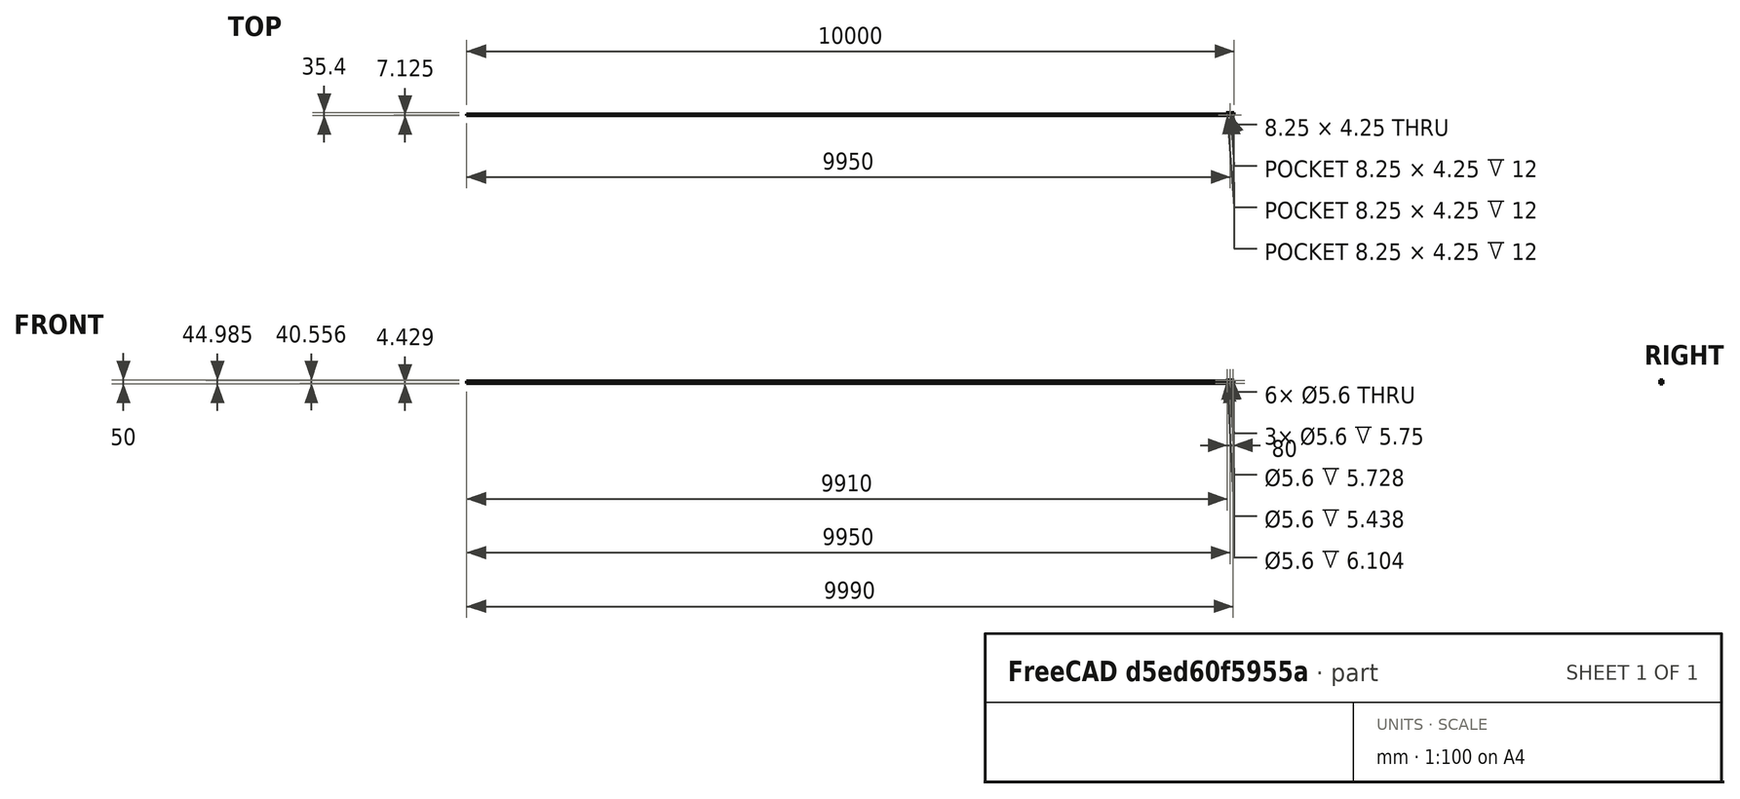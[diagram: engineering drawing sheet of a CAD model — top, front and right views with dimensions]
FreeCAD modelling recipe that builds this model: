
FCSTD DOCUMENT  (FreeCAD 0.16R)
Label: TubeHolder
License: All rights reserved
LicenseURL: http://en.wikipedia.org/wiki/All_rights_reserved
objects: Sketcher::SketchObject×5, PartDesign::Pocket×4, PartDesign::Chamfer×2, PartDesign::Pad×1, PartDesign::Fillet×1, Mesh::Feature×1
note: 18 computed .brp shape members not serialized (recipe doc carries the construction recipe); baked Part::Feature solids carry a one-line shape summary decoded from their .brp

FEATURE [Sketcher::SketchObject] Sketch
  sketch-geometry (10):
    g0: LineSegment StartX=-16.3948 StartY=10.4 StartZ=0 EndX=-22.3993 EndY=0 EndZ=0
    g1: LineSegment StartX=-22.3993 StartY=0 StartZ=0 EndX=22.3993 EndY=0 EndZ=0
    g2: LineSegment StartX=22.3993 StartY=0 StartZ=0 EndX=16.3948 EndY=10.4 EndZ=0
    g3: LineSegment StartX=16.3948 StartY=10.4 StartZ=0 EndX=50 EndY=10.4 EndZ=0
    g4: LineSegment StartX=50 StartY=10.4 StartZ=0 EndX=50 EndY=-25 EndZ=0
    g5: LineSegment StartX=50 StartY=-25 StartZ=0 EndX=-50 EndY=-25 EndZ=0
    g6: LineSegment StartX=-50 StartY=-25 StartZ=0 EndX=-50 EndY=10.4 EndZ=0
    g7: LineSegment StartX=-50 StartY=10.4 StartZ=0 EndX=-16.3948 EndY=10.4 EndZ=0
    g8: Circle CenterX=-16.9 CenterY=3.175 CenterZ=0 NormalX=0 NormalY=0 NormalZ=1 Radius=3.175
    g9: Circle CenterX=16.9 CenterY=3.175 CenterZ=0 NormalX=0 NormalY=0 NormalZ=1 Radius=3.175
  constraints (30):
    c: Coincident(g0,g1)
    c: Horizontal(g1)
    c: Coincident(g1,g2)
    c: Coincident(g2,g3)
    c: Horizontal(g3)
    c: Vertical(g4)
    c: Coincident(g4,g5)
    c: Horizontal(g5)
    c: Coincident(g5,g6)
    c: Coincident(g6,g7)
    c: Coincident(g7,g0)
    c: Horizontal(g7)
    c: Angle(g0) = -2.0944
    c: Angle(g2) = 2.0944
    c: PointOnObject(g-1,g1)
    c: Symmetric(g1,g0,g-1)
    c: Distance(g0,g7) = 10.4
    c: Distance(g1,g3) = 10.4
    c: Vertical(g6)
    c: Coincident(g4,g3)
    c: DistanceY(g4) = -25
    c: Symmetric(g3,g6,g-2)
    c: Distance(g6,g3) = 100
    c: Equal(g9,g8)
    c: Radius(g9) = 3.175
    c: Tangent(g9,g1)
    c: Tangent(g2,g9)
    c: Tangent(g8,g1)
    c: Tangent(g8,g0)
    c: Distance(g9,g8) = 33.8
FEATURE [PartDesign::Pad] Pad
  Length = 50
  Length2 = 100
  Sketch = -> Sketch
  Type = 0
FEATURE [Sketcher::SketchObject] Sketch001
  ExternalGeometry = -> [Pad]
  Placement = pos=(50,0,0) rot=(0.57735,0.57735,0.57735;2.0944rad)
  Support = -> Pad [Face5]
  sketch-geometry (3):
    g0: LineSegment StartX=-25 StartY=39.9699 StartZ=0 EndX=-9.44365 EndY=24.4135 EndZ=0
    g1: LineSegment StartX=-9.44365 StartY=24.4135 StartZ=0 EndX=-25 EndY=8.85716 EndZ=0
    g2: LineSegment StartX=-25 StartY=8.85716 StartZ=0 EndX=-25 EndY=39.9699 EndZ=0
  constraints (8):
    c: Coincident(g0,g1)
    c: Coincident(g1,g2)
    c: Coincident(g2,g0)
    c: Vertical(g2)
    c: Equal(g1,g0)
    c: Angle(g0,g1) = 1.5708
    c: PointOnObject(g0,g-3)
    c: Distance(g0) = 22
FEATURE [PartDesign::Pocket] Pocket
  Length = 5
  Sketch = -> Sketch001
  Type = 1
FEATURE [Sketcher::SketchObject] Sketch002
  ExternalGeometry = -> [Pocket]
  Placement = pos=(0,-25,0) rot=(1,0,0;1.5708rad)
  Support = -> Pocket [Face11]
  sketch-geometry (8):
    g0: Circle CenterX=-40 CenterY=44.9849 CenterZ=0 NormalX=0 NormalY=0 NormalZ=1 Radius=2.8
    g1: Circle CenterX=0 CenterY=44.9849 CenterZ=0 NormalX=0 NormalY=0 NormalZ=1 Radius=2.8
    g2: Circle CenterX=40 CenterY=44.9849 CenterZ=0 NormalX=0 NormalY=0 NormalZ=1 Radius=2.8
    g3: Circle CenterX=-40 CenterY=4.42858 CenterZ=0 NormalX=0 NormalY=0 NormalZ=1 Radius=2.8
    g4: Circle CenterX=0 CenterY=4.42858 CenterZ=0 NormalX=0 NormalY=0 NormalZ=1 Radius=2.8
    g5: Circle CenterX=40 CenterY=4.42858 CenterZ=0 NormalX=0 NormalY=0 NormalZ=1 Radius=2.8
    g6: LineSegment [constr] StartX=-50 StartY=44.9849 StartZ=0 EndX=50 EndY=44.9849 EndZ=0
    g7: LineSegment [constr] StartX=-50 StartY=4.42858 StartZ=0 EndX=50 EndY=4.42858 EndZ=0
  constraints (24):
    c: Radius(g2) = 2.8
    c: Equal(g2,g1)
    c: Equal(g2,g0)
    c: Equal(g2,g3)
    c: Equal(g2,g4)
    c: Equal(g2,g5)
    c: Horizontal(g6)
    c: Horizontal(g7)
    c: Symmetric(g-6,g-5,g7)
    c: Symmetric(g-4,g-3,g6)
    c: Symmetric(g-4,g-3,g6)
    c: Symmetric(g-6,g-5,g7)
    c: PointOnObject(g3,g7)
    c: PointOnObject(g4,g7)
    c: PointOnObject(g5,g7)
    c: PointOnObject(g2,g6)
    c: PointOnObject(g1,g6)
    c: PointOnObject(g0,g6)
    c: DistanceX(g2) = 40
    c: DistanceX(g0) = -40
    c: DistanceX(g3) = -40
    c: DistanceX(g5) = 40
    c: PointOnObject(g1,g-2)
    c: PointOnObject(g4,g-2)
FEATURE [PartDesign::Pocket] Pocket001
  Length = 15
  Sketch = -> Sketch002
  Type = 0
FEATURE [Sketcher::SketchObject] Sketch003
  Placement = pos=(0,0,50) rot=(0,0,1;0rad)
  Support = -> Pocket001 [Face5]
  sketch-geometry (12):
    g0: LineSegment StartX=-44.1 StartY=-15.438 StartZ=0 EndX=-35.85 EndY=-15.438 EndZ=0
    g1: LineSegment StartX=-35.85 StartY=-15.438 StartZ=0 EndX=-35.85 EndY=-19.688 EndZ=0
    g2: LineSegment StartX=-35.85 StartY=-19.688 StartZ=0 EndX=-44.1 EndY=-19.688 EndZ=0
    g3: LineSegment StartX=-44.1 StartY=-19.688 StartZ=0 EndX=-44.1 EndY=-15.438 EndZ=0
    g4: LineSegment StartX=-4.125 StartY=-15.728 StartZ=0 EndX=4.125 EndY=-15.728 EndZ=0
    g5: LineSegment StartX=4.125 StartY=-15.728 StartZ=0 EndX=4.125 EndY=-19.978 EndZ=0
    g6: LineSegment StartX=4.125 StartY=-19.978 StartZ=0 EndX=-4.125 EndY=-19.978 EndZ=0
    g7: LineSegment StartX=-4.125 StartY=-19.978 StartZ=0 EndX=-4.125 EndY=-15.728 EndZ=0
    g8: LineSegment StartX=35.85 StartY=-16.104 StartZ=0 EndX=44.1 EndY=-16.104 EndZ=0
    g9: LineSegment StartX=44.1 StartY=-16.104 StartZ=0 EndX=44.1 EndY=-20.354 EndZ=0
    g10: LineSegment StartX=44.1 StartY=-20.354 StartZ=0 EndX=35.85 EndY=-20.354 EndZ=0
    g11: LineSegment StartX=35.85 StartY=-20.354 StartZ=0 EndX=35.85 EndY=-16.104 EndZ=0
  constraints (33):
    c: Coincident(g0,g1)
    c: Coincident(g1,g2)
    c: Coincident(g2,g3)
    c: Coincident(g3,g0)
    c: Horizontal(g0)
    c: Horizontal(g2)
    c: Vertical(g1)
    c: Vertical(g3)
    c: Coincident(g4,g5)
    c: Coincident(g5,g6)
    c: Coincident(g6,g7)
    c: Coincident(g7,g4)
    c: Horizontal(g4)
    c: Horizontal(g6)
    c: Vertical(g5)
    c: Vertical(g7)
    c: Coincident(g8,g9)
    c: Coincident(g9,g10)
    c: Coincident(g10,g11)
    c: Coincident(g11,g8)
    c: Horizontal(g8)
    c: Horizontal(g10)
    c: Vertical(g9)
    c: Vertical(g11)
    c: Equal(g0,g4)
    c: Equal(g4,g8)
    c: Distance(g0) = 8.25
    c: Distance(g1) = 4.25
    c: Equal(g5,g1)
    c: Equal(g1,g11)
    c: Symmetric(g4,g4,g-2)
    c: DistanceX(g-1,g8) = 44.1
    c: DistanceX(g0) = -44.1
FEATURE [PartDesign::Pocket] Pocket002
  Length = 12
  Sketch = -> Sketch003
  Type = 0
FEATURE [Sketcher::SketchObject] Sketch004
  Placement = pos=(0,0,0) rot=(1,0,0;3.14159rad)
  Support = -> Pocket002 [Face4]
  sketch-geometry (12):
    g0: LineSegment StartX=-44.1 StartY=20 StartZ=0 EndX=-35.85 EndY=20 EndZ=0
    g1: LineSegment StartX=-35.85 StartY=20 StartZ=0 EndX=-35.85 EndY=15.75 EndZ=0
    g2: LineSegment StartX=-35.85 StartY=15.75 StartZ=0 EndX=-44.1 EndY=15.75 EndZ=0
    g3: LineSegment StartX=-44.1 StartY=15.75 StartZ=0 EndX=-44.1 EndY=20 EndZ=0
    g4: LineSegment StartX=-4.125 StartY=20 StartZ=0 EndX=4.125 EndY=20 EndZ=0
    g5: LineSegment StartX=4.125 StartY=20 StartZ=0 EndX=4.125 EndY=15.75 EndZ=0
    g6: LineSegment StartX=4.125 StartY=15.75 StartZ=0 EndX=-4.125 EndY=15.75 EndZ=0
    g7: LineSegment StartX=-4.125 StartY=15.75 StartZ=0 EndX=-4.125 EndY=20 EndZ=0
    g8: LineSegment StartX=35.85 StartY=20 StartZ=0 EndX=44.1 EndY=20 EndZ=0
    g9: LineSegment StartX=44.1 StartY=20 StartZ=0 EndX=44.1 EndY=15.75 EndZ=0
    g10: LineSegment StartX=44.1 StartY=15.75 StartZ=0 EndX=35.85 EndY=15.75 EndZ=0
    g11: LineSegment StartX=35.85 StartY=15.75 StartZ=0 EndX=35.85 EndY=20 EndZ=0
  constraints (36):
    c: Coincident(g0,g1)
    c: Coincident(g1,g2)
    c: Coincident(g2,g3)
    c: Coincident(g3,g0)
    c: Horizontal(g0)
    c: Horizontal(g2)
    c: Vertical(g1)
    c: Vertical(g3)
    c: Coincident(g4,g5)
    c: Coincident(g5,g6)
    c: Coincident(g6,g7)
    c: Coincident(g7,g4)
    c: Horizontal(g4)
    c: Horizontal(g6)
    c: Vertical(g5)
    c: Vertical(g7)
    c: Coincident(g8,g9)
    c: Coincident(g9,g10)
    c: Coincident(g10,g11)
    c: Coincident(g11,g8)
    c: Horizontal(g8)
    c: Horizontal(g10)
    c: Vertical(g9)
    c: Vertical(g11)
    c: Equal(g0,g4)
    c: Equal(g4,g8)
    c: Distance(g0) = 8.25
    c: Distance(g1) = 4.25
    c: Equal(g5,g1)
    c: Equal(g1,g11)
    c: Symmetric(g4,g4,g-2)
    c: DistanceX(g-1,g8) = 44.1
    c: DistanceX(g0) = -44.1
    c: DistanceY(g8) = 20
    c: DistanceY(g4) = 20
    c: DistanceY(g0) = 20
FEATURE [PartDesign::Pocket] Pocket003
  Length = 23
  Sketch = -> Sketch004
  Type = 0
FEATURE [PartDesign::Fillet] Fillet
  Base = -> Pocket003 [Edge2,Edge1,Edge49,Edge8,Edge123]
  Radius = 1
FEATURE [PartDesign::Chamfer] Chamfer
  Base = -> Fillet [Edge67,Edge68,Edge61,Edge69,Edge13,Edge70,Edge71,Edge38]
  Size = 1
FEATURE [PartDesign::Chamfer] Chamfer001
  Base = -> Chamfer [Edge34,Edge35,Edge36,Edge37,Edge38,Edge26,Edge39,Edge3]
  Size = 1
FEATURE [Mesh::Feature] Mesh  label="Chamfer001 (Meshed)"
